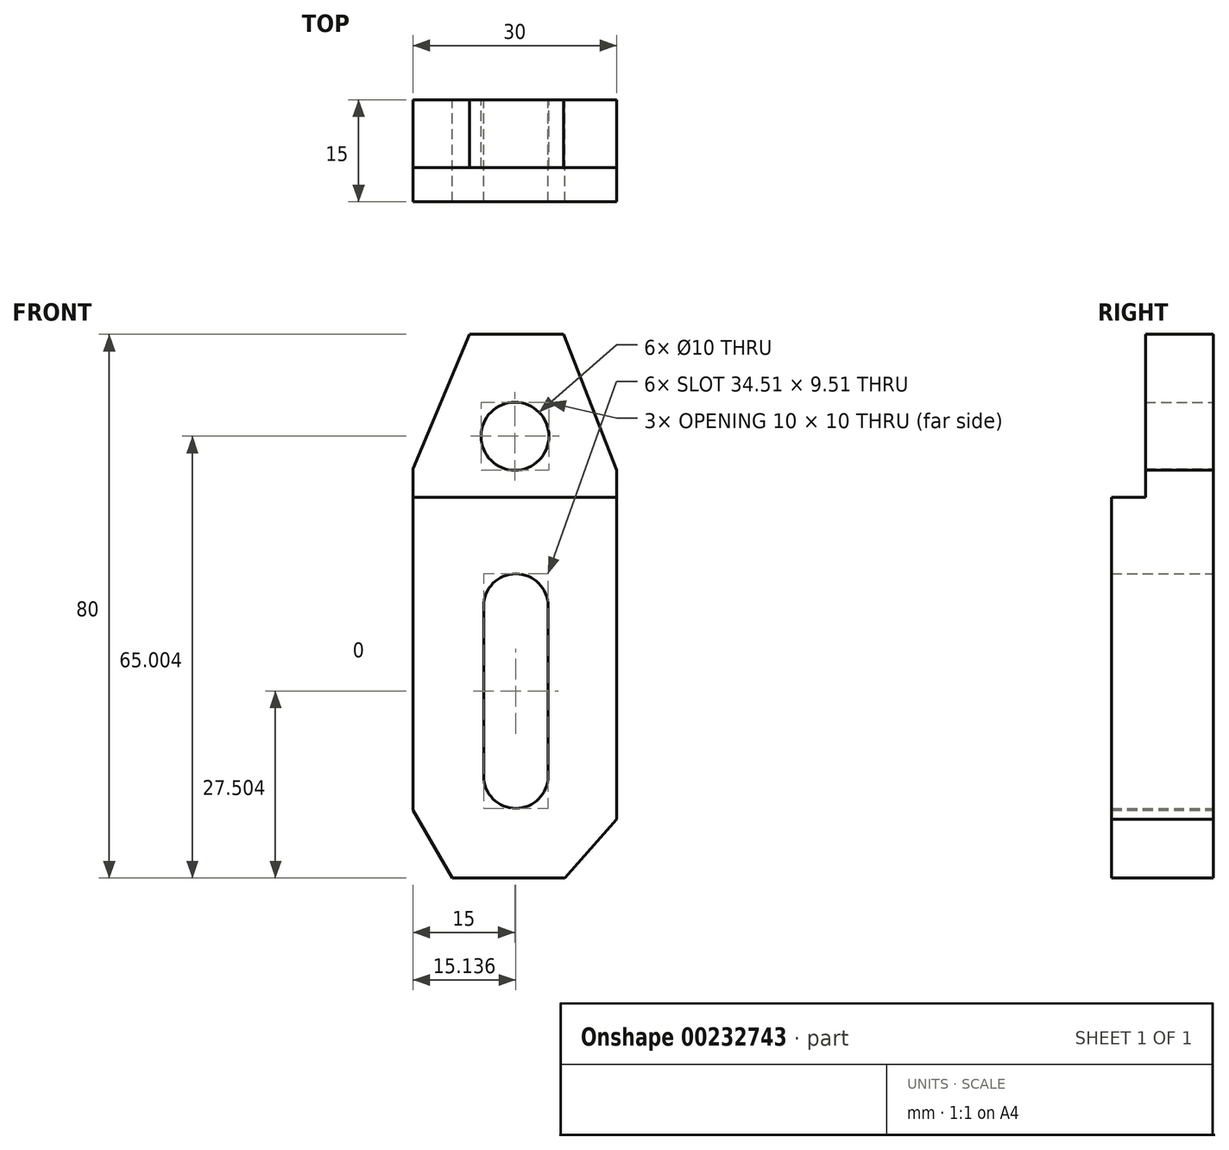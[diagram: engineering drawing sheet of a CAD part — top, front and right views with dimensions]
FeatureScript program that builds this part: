
annotation { "Feature Type Name" : "Feature", "Feature Type Description" : "" }
export const myFeature = defineFeature(function(context is Context, id is Id, definition is map)
    precondition{}
    {
        {
            var Q0;
            Q0=qCreatedBy(makeId("Front.planeOp"),FACE);
            var sketch = newSketch(context, id + "F0", { "sketchPlane" : qUnion([Q0])});
            skLineSegment(sketch, "E0", {"start": v(0, 37.58) * mm, "end": v(0, -40.2) * mm, "construction": true});
            skLineSegment(sketch, "E1", {"start": v(-47.65, 0) * mm, "end": v(54.75, 0) * mm, "construction": true});
            skLineSegment(sketch, "E2.bottom", {"start": v(7.33, -50.24) * mm, "end": v(-9.23, -50.24) * mm});
            skLineSegment(sketch, "E2.top", {"start": v(7.15, 29.76) * mm, "end": v(-6.66, 29.76) * mm});
            skLineSegment(sketch, "E2.left", {"start": v(15, -41.6) * mm, "end": v(15, 9.76) * mm});
            skLineSegment(sketch, "E2.right", {"start": v(-15, -40.24) * mm, "end": v(-15, 9.96) * mm});
            skPoint(sketch, "E2.middle", {"position": v(0, -10.24) * mm});
            skLineSegment(sketch, "E3", {"start": v(-15, -40.24) * mm, "end": v(-9.23, -50.24) * mm});
            skLineSegment(sketch, "E4", {"start": v(7.33, -50.24) * mm, "end": v(15, -41.6) * mm});
            skLineSegment(sketch, "E5.bottom", {"start": v(0, -10.24) * mm, "end": v(0.14, -10.24) * mm});
            skLineSegment(sketch, "E5.top", {"start": v(0, -35.24) * mm, "end": v(0.14, -35.24) * mm});
            skLineSegment(sketch, "E5.left", {"start": v(-4.62, -10.24) * mm, "end": v(-4.62, -35.24) * mm});
            skLineSegment(sketch, "E5.right", {"start": v(4.89, -10.24) * mm, "end": v(4.89, -35.24) * mm});
            skArc(sketch, "E6", {"start": v(4.89, -10.24) * mm, "mid": v(0.14, -5.48) * mm, "end": v(-4.62, -10.24) * mm});
            skArc(sketch, "E7", {"start": v(-4.62, -35.24) * mm, "mid": v(0.14, -39.99) * mm, "end": v(4.89, -35.24) * mm});
            skCircle(sketch, "E8", {"center": v(0, 14.76) * mm, "radius": 5 * mm});
            skLineSegment(sketch, "E9", {"start": v(-6.66, 29.76) * mm, "end": v(-15, 9.96) * mm});
            skLineSegment(sketch, "E10", {"start": v(7.15, 29.76) * mm, "end": v(15, 9.76) * mm});
            skPoint(sketch, "E11.orphan", {"position": v(-15, 29.76) * mm});
            skPoint(sketch, "E12.orphan", {"position": v(15, 29.76) * mm});
            skPoint(sketch, "E13.orphan", {"position": v(15, -50.24) * mm});
            skPoint(sketch, "E14.orphan", {"position": v(-15, -50.24) * mm});
            skSolve(sketch);
        }
        {
            var Q0;
            Q0=makeQuery(id+"F0.imprint","IMPRINT",FACE,{"disambiguationData":[TD([[makeQuery(id+"F0.imprint","IMPRINT",EDGE,{"derivedFrom":sQuery(id+"F0.wireOp",EDGE,"E2.bottom")}),-1.0]])]});
            extrude(context, id + "F1", {"entities" : qUnion([Q0]), "depth" : 15 * mm});
        }
        {
            var Q0;
            Q0=qCreatedBy(makeId("Right.planeOp"),FACE);
            var sketch = newSketch(context, id + "F2", { "sketchPlane" : qUnion([Q0])});
            skLineSegment(sketch, "E15.0", {"start": v(-15, -50.24) * mm, "end": v(0, -50.24) * mm});
            skLineSegment(sketch, "E16.0", {"start": v(-15, -41.6) * mm, "end": v(-15, 9.76) * mm});
            skLineSegment(sketch, "E17.0", {"start": v(-15, -50.24) * mm, "end": v(-15, -41.6) * mm});
            skPoint(sketch, "E18.0", {"position": v(0, -45.92) * mm});
            skPoint(sketch, "E19.0", {"position": v(0, -10.24) * mm});
            skLineSegment(sketch, "E20.0.0", {"start": v(0, -41.6) * mm, "end": v(0, 9.76) * mm});
            skLineSegment(sketch, "E20.0.2", {"start": v(-15, 9.76) * mm, "end": v(-15, -41.6) * mm});
            skLineSegment(sketch, "E20.0.3", {"start": v(-15, -41.6) * mm, "end": v(0, -41.6) * mm});
            skLineSegment(sketch, "E21.bottom", {"start": v(-15, 5.76) * mm, "end": v(-10, 5.76) * mm});
            skLineSegment(sketch, "E21.top", {"start": v(-15, 39.44) * mm, "end": v(-10, 39.44) * mm});
            skLineSegment(sketch, "E21.right", {"start": v(-10, 5.76) * mm, "end": v(-10, 39.44) * mm});
            skLineSegment(sketch, "E22", {"start": v(-15, 39.44) * mm, "end": v(-15, 5.76) * mm});
            skSolve(sketch);
        }
        {
            var Q0;
            Q0 = qSketchRegion(id + "F2", true);
            extrude(context, id + "F3", {"entities" : qUnion([Q0]), "operationType" : NewBodyOperationType.REMOVE, "endBound" : BoundingType.SYMMETRIC, "oppositeDirection" : true, "depth" : 50 * mm});
        }
    });
